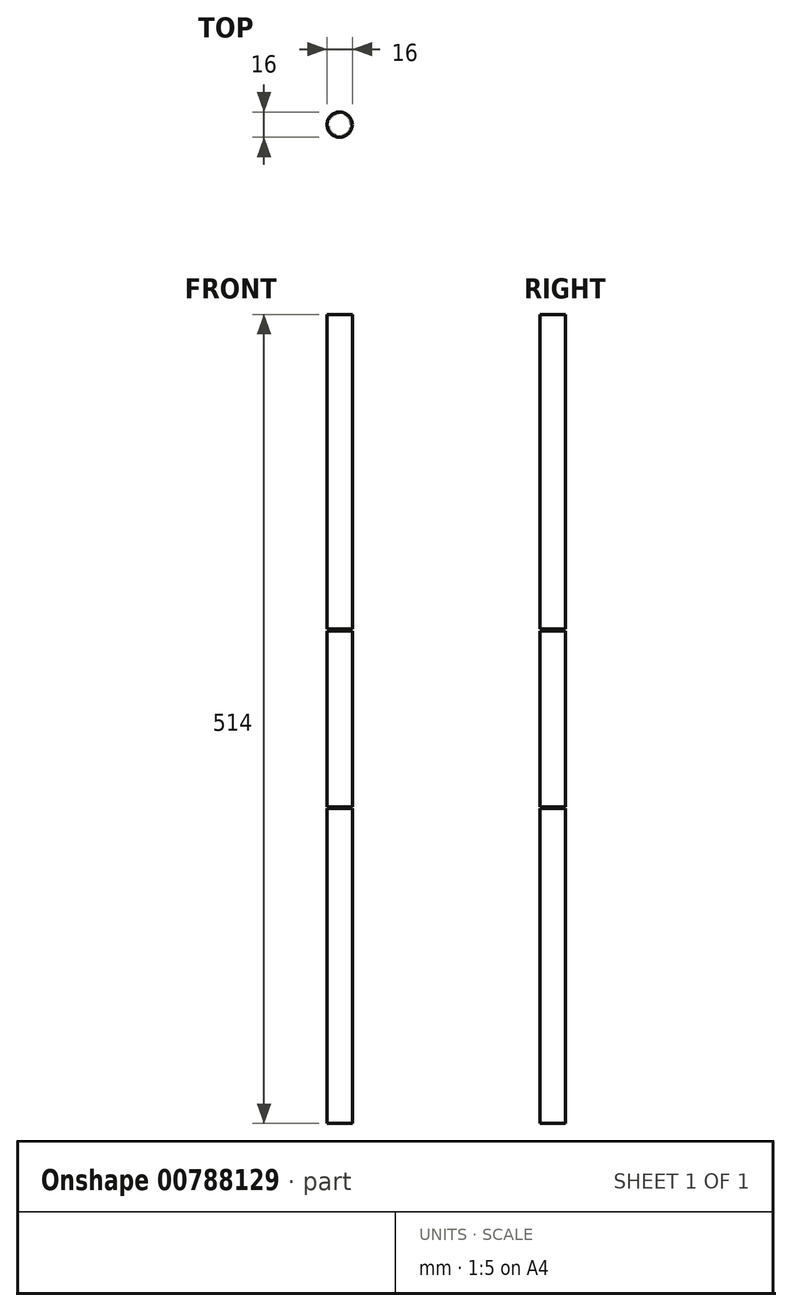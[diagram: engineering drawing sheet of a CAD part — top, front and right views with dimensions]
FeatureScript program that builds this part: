
annotation { "Feature Type Name" : "Feature", "Feature Type Description" : "" }
export const myFeature = defineFeature(function(context is Context, id is Id, definition is map)
    precondition{}
    {
        {
            var Q0;
            Q0=qCreatedBy(makeId("Front.planeOp"),FACE);
            var sketch = newSketch(context, id + "F0", { "sketchPlane" : qUnion([Q0])});
            skLineSegment(sketch, "E0", {"start": v(0, 514) * mm, "end": v(-8, 514) * mm});
            skLineSegment(sketch, "E1", {"start": v(-8, 514) * mm, "end": v(-8, 314) * mm});
            skLineSegment(sketch, "E2", {"start": v(-8, 314) * mm, "end": v(-7, 314) * mm});
            skLineSegment(sketch, "E3", {"start": v(-7, 314) * mm, "end": v(-7, 313) * mm});
            skLineSegment(sketch, "E4", {"start": v(-7, 313) * mm, "end": v(-8, 313) * mm});
            skLineSegment(sketch, "E5", {"start": v(-8, 313) * mm, "end": v(-8, 201) * mm});
            skLineSegment(sketch, "E6", {"start": v(-8, 201) * mm, "end": v(-7, 201) * mm});
            skLineSegment(sketch, "E7", {"start": v(-7, 201) * mm, "end": v(-7, 200) * mm});
            skLineSegment(sketch, "E8", {"start": v(-7, 200) * mm, "end": v(-8, 200) * mm});
            skLineSegment(sketch, "E9", {"start": v(-8, 200) * mm, "end": v(-8, 125.63) * mm});
            skLineSegment(sketch, "E10", {"start": v(-8, 0) * mm, "end": v(0, 0) * mm});
            skLineSegment(sketch, "E11", {"start": v(0, 0) * mm, "end": v(0, 514) * mm});
            skLineSegment(sketch, "E12.trimOffspring", {"start": v(-8, 125.63) * mm, "end": v(-8, 99) * mm});
            skLineSegment(sketch, "E13.trimOffspring", {"start": v(-8, 99) * mm, "end": v(-8, 0) * mm});
            skLineSegment(sketch, "E14", {"start": v(0, -69.12) * mm, "end": v(0, 370.22) * mm, "construction": true});
            skPoint(sketch, "E15.orphan", {"position": v(-8, 100) * mm});
            skSolve(sketch);
        }
        {
            var Q0;
            Q0 = qSketchRegion(id + "F0", true);
            var Q1;
            Q1=sQuery(id+"F0.wireOp",EDGE,"E14");
            revolve(context, id + "F1", {"surfaceOperationType" : NewSurfaceOperationType.NEW, "entities" : qUnion([Q0]), "axis" : qUnion([Q1]), "revolveType" : RevolveType.FULL});
        }
    });
